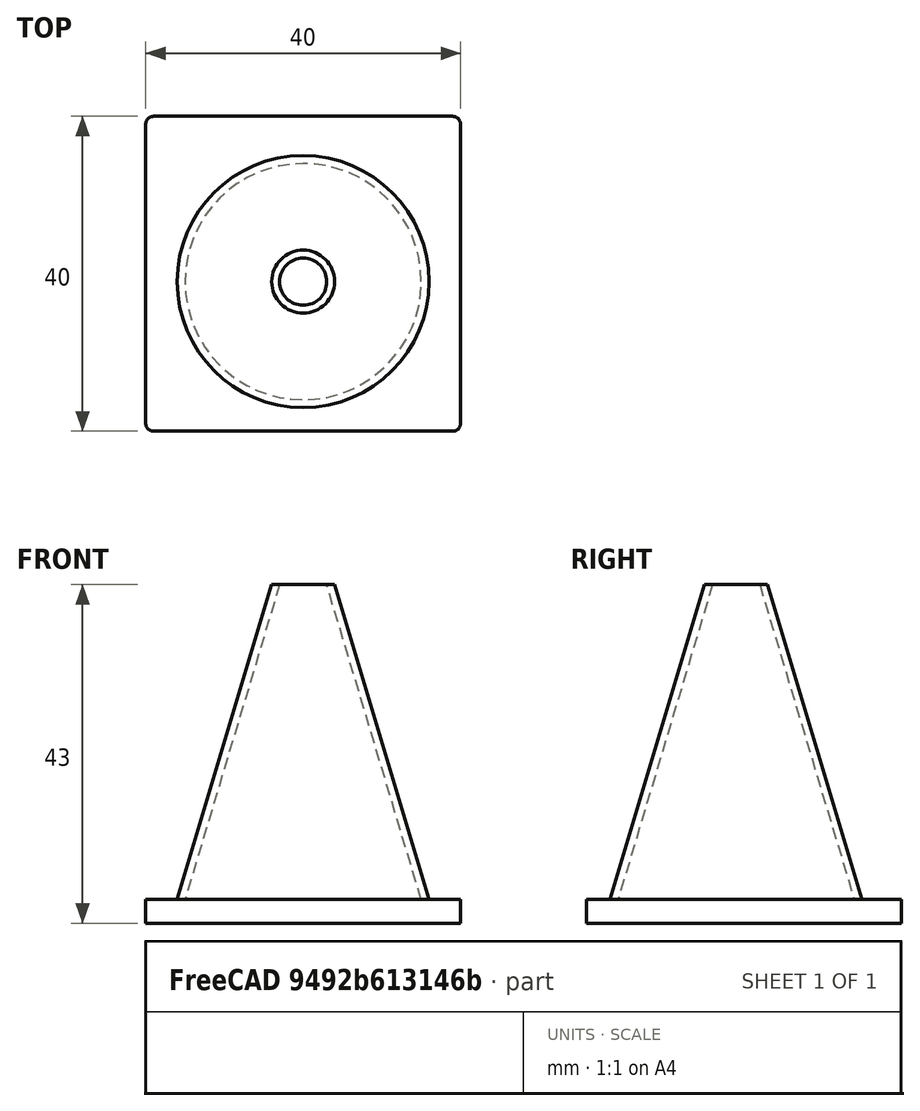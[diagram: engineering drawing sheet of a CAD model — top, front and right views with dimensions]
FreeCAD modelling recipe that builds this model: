
FCSTD DOCUMENT  (FreeCAD 0.21R33694 (Git))
Label: OJT1_T14P02_con
License: All rights reserved
LicenseURL: http://en.wikipedia.org/wiki/All_rights_reserved
objects: Part::Cone×2, Part::Box×1, Part::Cut×1, Part::Fillet×1, Part::Fuse×1
note: 6 computed .brp shape members not serialized (recipe doc carries the construction recipe); baked Part::Feature solids carry a one-line shape summary decoded from their .brp

FEATURE [Part::Cone] Cone
  Angle = 360
  AttacherType = Attacher::AttachEngine3D
  Height = 40
  Radius1 = 16
  Radius2 = 4
FEATURE [Part::Cone] Cone001
  Angle = 360
  AttacherType = Attacher::AttachEngine3D
  Height = 40
  Radius1 = 15
  Radius2 = 3
FEATURE [Part::Box] Box  label="Cube"
  AttacherType = Attacher::AttachEngine3D
  Height = 3
  Length = 40
  Placement = pos=(0,0,-3) rot=(0,0,1;0rad)
  Width = 40
FEATURE [Part::Cut] Cut
  Base = -> Cone
  Refine = true
  Tool = -> Cone001
FEATURE [Part::Fillet] Fillet
  Base = -> Box
  Edges = 4 edges r=1: [Edge1,Edge3,Edge5,Edge7]
  Placement = pos=(-20,-19,0) rot=(0,0,1;0rad)
FEATURE [Part::Fuse] Fusion
  Base = -> Cut
  Refine = true
  Tool = -> Fillet
